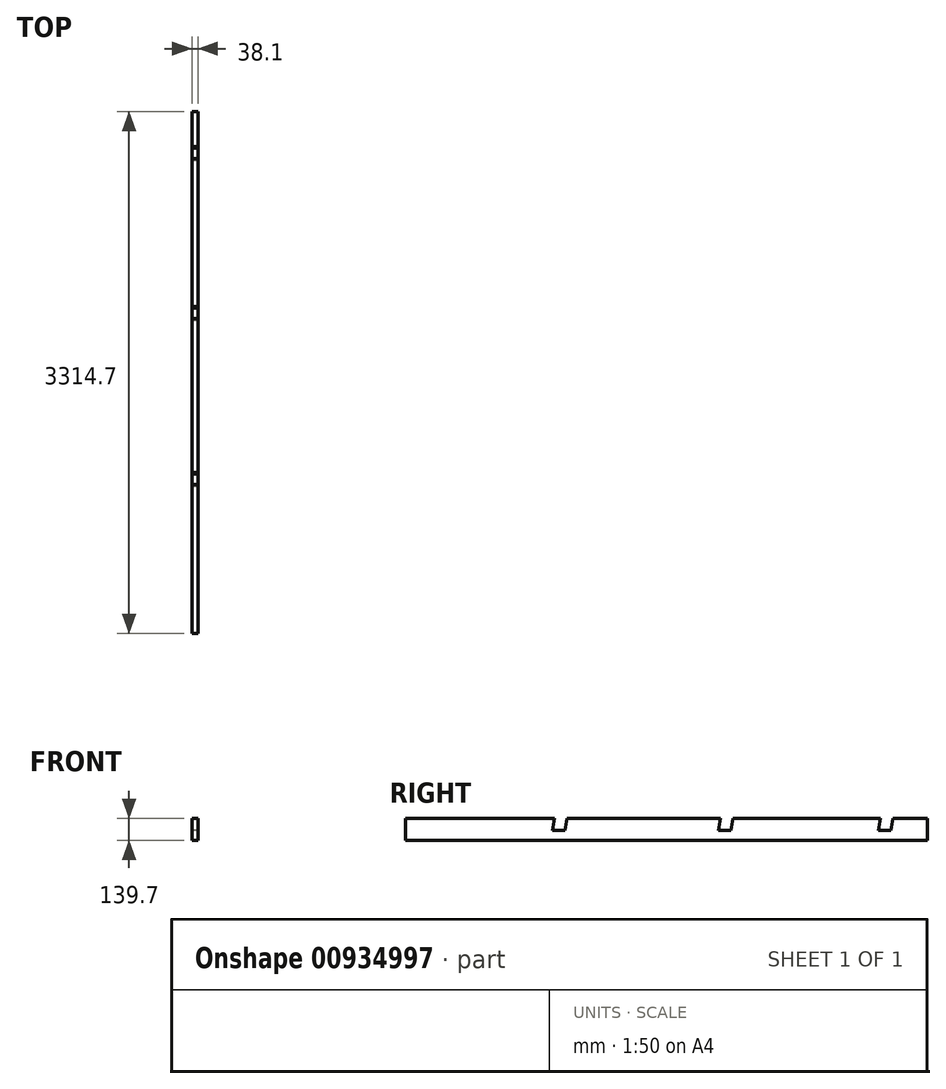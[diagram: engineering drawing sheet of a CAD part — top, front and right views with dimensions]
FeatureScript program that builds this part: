
annotation { "Feature Type Name" : "Feature", "Feature Type Description" : "" }
export const myFeature = defineFeature(function(context is Context, id is Id, definition is map)
    precondition{}
    {
        {
            var Q0;
            Q0=qCreatedBy(makeId("Front.planeOp"),FACE);
            var sketch = newSketch(context, id + "F0", { "sketchPlane" : qUnion([Q0])});
            skLineSegment(sketch, "E0.bottom", {"start": v(19.05, -69.85) * mm, "end": v(-19.05, -69.85) * mm});
            skLineSegment(sketch, "E0.top", {"start": v(19.05, 69.85) * mm, "end": v(-19.05, 69.85) * mm});
            skLineSegment(sketch, "E0.left", {"start": v(19.05, -69.85) * mm, "end": v(19.05, 69.85) * mm});
            skLineSegment(sketch, "E0.right", {"start": v(-19.05, -69.85) * mm, "end": v(-19.05, 69.85) * mm});
            skPoint(sketch, "E0.middle", {"position": v(0, 0) * mm});
            skSolve(sketch);
        }
        {
            var Q0;
            Q0 = qSketchRegion(id + "F0", true);
            extrude(context, id + "F1", {"entities" : qUnion([Q0]), "depth" : 3314.7 * mm, "offsetDistance" : 25.4 * mm, "symmetric" : true});
        }
        {
            var Q0;
            Q0=qCreatedBy(makeId("Right.planeOp"),FACE);
            var sketch = newSketch(context, id + "F2", { "sketchPlane" : qUnion([Q0])});
            skLineSegment(sketch, "E1.bottom", {"start": v(-711.2, 69.85) * mm, "end": v(-633.99, 69.85) * mm});
            skLineSegment(sketch, "E1.top", {"start": v(-723.51, -5.35) * mm, "end": v(-646.3, -5.35) * mm});
            skLineSegment(sketch, "E1.left", {"start": v(-711.2, 69.85) * mm, "end": v(-723.51, -5.35) * mm});
            skLineSegment(sketch, "E1.right", {"start": v(-633.99, 69.85) * mm, "end": v(-646.3, -5.35) * mm});
            skLineSegment(sketch, "E2.bottom", {"start": v(342.9, 69.85) * mm, "end": v(420.11, 69.85) * mm});
            skLineSegment(sketch, "E2.top", {"start": v(330.59, -5.35) * mm, "end": v(407.8, -5.35) * mm});
            skLineSegment(sketch, "E2.left", {"start": v(342.9, 69.85) * mm, "end": v(330.59, -5.35) * mm});
            skLineSegment(sketch, "E2.right", {"start": v(420.11, 69.85) * mm, "end": v(407.8, -5.35) * mm});
            skLineSegment(sketch, "E3.bottom", {"start": v(1358.9, 69.85) * mm, "end": v(1436.11, 69.85) * mm});
            skLineSegment(sketch, "E3.top", {"start": v(1346.59, -5.35) * mm, "end": v(1423.8, -5.35) * mm});
            skLineSegment(sketch, "E3.left", {"start": v(1358.9, 69.85) * mm, "end": v(1346.59, -5.35) * mm});
            skLineSegment(sketch, "E3.right", {"start": v(1436.11, 69.85) * mm, "end": v(1423.8, -5.35) * mm});
            skSolve(sketch);
        }
        {
            var Q0;
            Q0 = qSketchRegion(id + "F2", true);
            extrude(context, id + "F3", {"entities" : qUnion([Q0]), "operationType" : NewBodyOperationType.REMOVE, "depth" : 254 * mm, "offsetDistance" : 25.4 * mm, "symmetric" : true});
        }
    });
